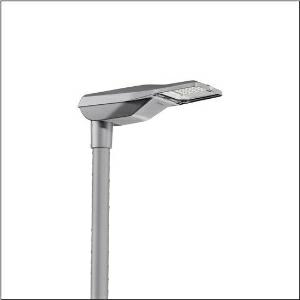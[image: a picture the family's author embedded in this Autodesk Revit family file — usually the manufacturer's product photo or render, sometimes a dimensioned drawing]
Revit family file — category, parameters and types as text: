
# Revit family: streetlight_sl_21_iq_micro___stw1_0a_5xe1e21g08cb_2b52
name_source: partatom
category: Lighting Fixtures
units: mm (PartAtom-declared; Revit-internal decimal feet)

## family parameters
Cut with Voids When Loaded = No
Host = Face
Light Source = No
Part Type = Normal
Room Calculation Point = No
Round Connector Dimension = Use Diameter
Shared = No

## types (1)
- --- (1 x LED, 2380 lm, 19.4 W, 2200K)
    Apparent Load = 19 VA
    CIE Flux Codes = 38 75 98 100 100
    Color Rendering = 70
    Color Temperature = 2200K
    Default Elevation = 1800 mm
    Description = Streetlight SL 21 iQ micro, mast luminaire, primary light control with lens, of PMMA, primary optical cover: cover, of toughened safety glass, transparent, light distribution: STW1.0a, light emission: direct distribution, primary light characteristic: asymmetric, installation type: post-top, side-entry, LED, High Power LED, rated luminous flux: 2.380lm, luminous efficacy: 123lm/W, light colour: 722, colour temperature: 2200K, control gear: iQ Street-Remote, control: Street-Remote, Auto-Match, Temp-Guard, Lumen-Switch, Night-Set, Smart-Wire, Light-Fading, Desk-Remote (wireless, voltage-free reading and setting of iQ features in the workshop via application-optimized NFC function/RFID function), optimised constant luminous flux control (CLO 2.0), pre-setting: linear dimming characteristic, mains connection: 220..240V, AC, 50/60Hz, start of lifetime: 19W, end of service life: 20W, reduction: 10W, luminaire housing, of diecast aluminium, powder-coated, Siteco® metallic grey (DB 702S), corrosivity category C5 mid according to DIN EN ISO 12944, please order mast flange separately, inclination adjustable: 0°, 5°, 10°, 15°, sealing non-destructively replaceable, multi-level sealing system, length: 528mm, width: 235mm, height: 110mm, mast flange for spigot size: 42mm (side-entry): 5XC10008XM4, 60/48mm (side-entry/post-top): 5XC10108XM2, 76/60mm (side-entry/post-top): 5XC10108XM1, protection rating (complete): IP66, insulation class (complete): insulation class II (safety insulation), certification: CE, ENEC, ENEC+, VDE, impact resistance: IK10, permissible operating ambient temperature for outdoor applications: -40..+50°C, standard-compliant lighting for roads and squares, packaging unit: 1 piece

Light Distribution: STW1.0a
    Height = 110 mm
    Lamp = 1 x LED
    Lamp Light Flux = 2380 lm
    Lamp Power = 19.4 W
    Lamp count = 1
    Length = 528 mm
    Luminous efficacy = 123 lm/W
    Manufacturer = Siteco
    ModVariant = No
    Model = 5XE1E21G08CB
    Number of Poles = 1
    OnlyDefault = Yes
    Power Factor = 1
    Product Name = Streetlight SL 21 iQ micro | STW1.0a
    Product group = mast luminaire | pylon top
    ProductGroupID = 6100
    Protection Class = Protection class II
    Protection Degree = IP 66
    RLX_Detail_Level = 1
    RLX_Emergency_Light_Flux = 0 lm
    RLX_Emergency_Type = 0
    RLX_Emergency_Type_DB = No
    RlxData = <blob elided: 98505 chars, md5=66e364d2>
    Socket = socket
    Standby Power = 0 W
    System Light Flux = 2380 lm
    System Power = 19 W
    Type Comments = factory setting: luminous flux: 100 % | dim-lin: 254 | 387 mA
    Type Image = l_1006881.jpg
    URL = http://relux.com
    VarID = @adj_160411
    Voltage = 0 V
    Weight = 0.00 kg
    Width = 235 mm

## geometry (parser evidence)
native form markers: Blend x4, Sweep x11
no freeform markers — native parametric forms only
